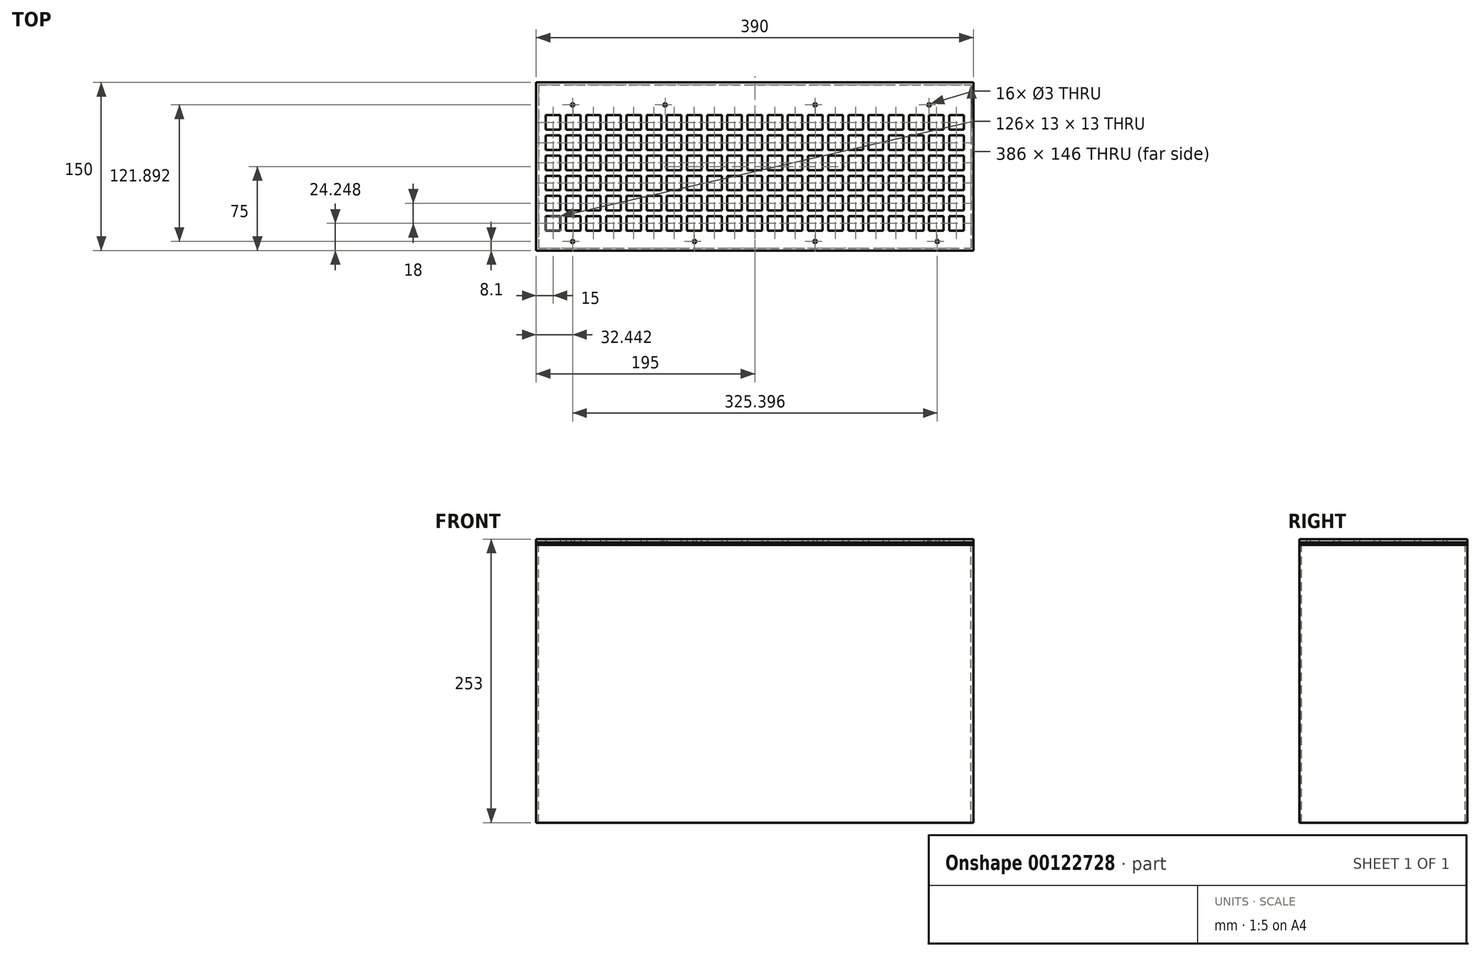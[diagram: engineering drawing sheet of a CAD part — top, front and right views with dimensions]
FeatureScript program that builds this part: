
annotation { "Feature Type Name" : "Feature", "Feature Type Description" : "" }
export const myFeature = defineFeature(function(context is Context, id is Id, definition is map)
    precondition{}
    {
        {
            var Q0;
            Q0=qCreatedBy(makeId("Top.planeOp"),FACE);
            var sketch = newSketch(context, id + "F0", { "sketchPlane" : qUnion([Q0])});
            skLineSegment(sketch, "E0.bottom", {"start": v(0, 0) * mm, "end": v(390, 0) * mm});
            skLineSegment(sketch, "E0.top", {"start": v(0, -150) * mm, "end": v(390, -150) * mm});
            skLineSegment(sketch, "E0.left", {"start": v(0, 0) * mm, "end": v(0, -150) * mm});
            skLineSegment(sketch, "E0.right", {"start": v(390, 0) * mm, "end": v(390, -150) * mm});
            skLineSegment(sketch, "E1.bottom", {"start": v(8.5, -29.25) * mm, "end": v(21.5, -29.25) * mm});
            skLineSegment(sketch, "E1.top", {"start": v(8.5, -42.25) * mm, "end": v(21.5, -42.25) * mm});
            skLineSegment(sketch, "E1.left", {"start": v(8.5, -29.25) * mm, "end": v(8.5, -42.25) * mm});
            skLineSegment(sketch, "E1.right", {"start": v(21.5, -29.25) * mm, "end": v(21.5, -42.25) * mm});
            skLineSegment(sketch, "E2.bottom", {"start": v(8.5, -47.25) * mm, "end": v(21.5, -47.25) * mm});
            skLineSegment(sketch, "E2.top", {"start": v(8.5, -60.25) * mm, "end": v(21.5, -60.25) * mm});
            skLineSegment(sketch, "E2.left", {"start": v(8.5, -47.25) * mm, "end": v(8.5, -60.25) * mm});
            skLineSegment(sketch, "E2.right", {"start": v(21.5, -47.25) * mm, "end": v(21.5, -60.25) * mm});
            skLineSegment(sketch, "E3.bottom", {"start": v(8.5, -65.25) * mm, "end": v(21.5, -65.25) * mm});
            skLineSegment(sketch, "E3.top", {"start": v(8.5, -78.25) * mm, "end": v(21.5, -78.25) * mm});
            skLineSegment(sketch, "E3.left", {"start": v(8.5, -65.25) * mm, "end": v(8.5, -78.25) * mm});
            skLineSegment(sketch, "E3.right", {"start": v(21.5, -65.25) * mm, "end": v(21.5, -78.25) * mm});
            skLineSegment(sketch, "E4.bottom", {"start": v(8.5, -83.25) * mm, "end": v(21.5, -83.25) * mm});
            skLineSegment(sketch, "E4.top", {"start": v(8.5, -96.25) * mm, "end": v(21.5, -96.25) * mm});
            skLineSegment(sketch, "E4.left", {"start": v(8.5, -83.25) * mm, "end": v(8.5, -96.25) * mm});
            skLineSegment(sketch, "E4.right", {"start": v(21.5, -83.25) * mm, "end": v(21.5, -96.25) * mm});
            skLineSegment(sketch, "E5.bottom", {"start": v(8.5, -101.25) * mm, "end": v(21.5, -101.25) * mm});
            skLineSegment(sketch, "E5.top", {"start": v(8.5, -114.25) * mm, "end": v(21.5, -114.25) * mm});
            skLineSegment(sketch, "E5.left", {"start": v(8.5, -101.25) * mm, "end": v(8.5, -114.25) * mm});
            skLineSegment(sketch, "E5.right", {"start": v(21.5, -101.25) * mm, "end": v(21.5, -114.25) * mm});
            skLineSegment(sketch, "E6.bottom", {"start": v(8.5, -119.25) * mm, "end": v(21.5, -119.25) * mm});
            skLineSegment(sketch, "E6.top", {"start": v(8.5, -132.25) * mm, "end": v(21.5, -132.25) * mm});
            skLineSegment(sketch, "E6.left", {"start": v(8.5, -119.25) * mm, "end": v(8.5, -132.25) * mm});
            skLineSegment(sketch, "E6.right", {"start": v(21.5, -119.25) * mm, "end": v(21.5, -132.25) * mm});
            skLineSegment(sketch, "E7", {"start": v(24, -21.56) * mm, "end": v(24, -144.75) * mm, "construction": true});
            skLineSegment(sketch, "E8.MirrorCS", {"start": v(39.5, -47.25) * mm, "end": v(39.5, -60.25) * mm});
            skLineSegment(sketch, "E9.MirrorCS", {"start": v(39.5, -60.25) * mm, "end": v(26.5, -60.25) * mm});
            skLineSegment(sketch, "E10.MirrorCS", {"start": v(39.5, -132.25) * mm, "end": v(26.5, -132.25) * mm});
            skLineSegment(sketch, "E11.MirrorCS", {"start": v(39.5, -119.25) * mm, "end": v(26.5, -119.25) * mm});
            skLineSegment(sketch, "E12.MirrorCS", {"start": v(39.5, -119.25) * mm, "end": v(39.5, -132.25) * mm});
            skLineSegment(sketch, "E13.MirrorCS", {"start": v(26.5, -29.25) * mm, "end": v(26.5, -42.25) * mm});
            skLineSegment(sketch, "E14.MirrorCS", {"start": v(39.5, -29.25) * mm, "end": v(26.5, -29.25) * mm});
            skLineSegment(sketch, "E15.MirrorCS", {"start": v(39.5, -101.25) * mm, "end": v(26.5, -101.25) * mm});
            skLineSegment(sketch, "E16.MirrorCS", {"start": v(26.5, -83.25) * mm, "end": v(26.5, -96.25) * mm});
            skLineSegment(sketch, "E17.MirrorCS", {"start": v(39.5, -83.25) * mm, "end": v(39.5, -96.25) * mm});
            skLineSegment(sketch, "E18.MirrorCS", {"start": v(39.5, -96.25) * mm, "end": v(26.5, -96.25) * mm});
            skLineSegment(sketch, "E19.MirrorCS", {"start": v(39.5, -83.25) * mm, "end": v(26.5, -83.25) * mm});
            skLineSegment(sketch, "E20.MirrorCS", {"start": v(26.5, -65.25) * mm, "end": v(26.5, -78.25) * mm});
            skLineSegment(sketch, "E21.MirrorCS", {"start": v(39.5, -65.25) * mm, "end": v(39.5, -78.25) * mm});
            skLineSegment(sketch, "E22.MirrorCS", {"start": v(39.5, -65.25) * mm, "end": v(26.5, -65.25) * mm});
            skLineSegment(sketch, "E23.MirrorCS", {"start": v(39.5, -78.25) * mm, "end": v(26.5, -78.25) * mm});
            skLineSegment(sketch, "E24.MirrorCS", {"start": v(26.5, -101.25) * mm, "end": v(26.5, -114.25) * mm});
            skLineSegment(sketch, "E25.MirrorCS", {"start": v(26.5, -47.25) * mm, "end": v(26.5, -60.25) * mm});
            skLineSegment(sketch, "E26.MirrorCS", {"start": v(26.5, -119.25) * mm, "end": v(26.5, -132.25) * mm});
            skLineSegment(sketch, "E27.MirrorCS", {"start": v(39.5, -101.25) * mm, "end": v(39.5, -114.25) * mm});
            skLineSegment(sketch, "E28.MirrorCS", {"start": v(39.5, -29.25) * mm, "end": v(39.5, -42.25) * mm});
            skLineSegment(sketch, "E29.MirrorCS", {"start": v(39.5, -114.25) * mm, "end": v(26.5, -114.25) * mm});
            skLineSegment(sketch, "E30.MirrorCS", {"start": v(39.5, -47.25) * mm, "end": v(26.5, -47.25) * mm});
            skLineSegment(sketch, "E31.MirrorCS", {"start": v(39.5, -42.25) * mm, "end": v(26.5, -42.25) * mm});
            skLineSegment(sketch, "E32", {"start": v(42, -21.56) * mm, "end": v(42, -144.75) * mm, "construction": true});
            skLineSegment(sketch, "E33.MirrorCS", {"start": v(57.5, -119.25) * mm, "end": v(57.5, -132.25) * mm});
            skLineSegment(sketch, "E34.MirrorCS", {"start": v(44.5, -29.25) * mm, "end": v(44.5, -42.25) * mm});
            skLineSegment(sketch, "E35.MirrorCS", {"start": v(44.5, -119.25) * mm, "end": v(44.5, -132.25) * mm});
            skLineSegment(sketch, "E36.MirrorCS", {"start": v(44.5, -114.25) * mm, "end": v(57.5, -114.25) * mm});
            skLineSegment(sketch, "E37.MirrorCS", {"start": v(75.5, -83.25) * mm, "end": v(75.5, -96.25) * mm});
            skLineSegment(sketch, "E38.MirrorCS", {"start": v(62.5, -65.25) * mm, "end": v(62.5, -78.25) * mm});
            skLineSegment(sketch, "E39.MirrorCS", {"start": v(75.5, -114.25) * mm, "end": v(62.5, -114.25) * mm});
            skLineSegment(sketch, "E40.MirrorCS", {"start": v(75.5, -42.25) * mm, "end": v(62.5, -42.25) * mm});
            skLineSegment(sketch, "E41.MirrorCS", {"start": v(57.5, -83.25) * mm, "end": v(57.5, -96.25) * mm});
            skLineSegment(sketch, "E42.MirrorCS", {"start": v(75.5, -101.25) * mm, "end": v(75.5, -114.25) * mm});
            skLineSegment(sketch, "E43.MirrorCS", {"start": v(75.5, -29.25) * mm, "end": v(75.5, -42.25) * mm});
            skLineSegment(sketch, "E44.MirrorCS", {"start": v(44.5, -83.25) * mm, "end": v(44.5, -96.25) * mm});
            skLineSegment(sketch, "E45.MirrorCS", {"start": v(44.5, -96.25) * mm, "end": v(57.5, -96.25) * mm});
            skLineSegment(sketch, "E46.MirrorCS", {"start": v(62.5, -101.25) * mm, "end": v(62.5, -114.25) * mm});
            skLineSegment(sketch, "E47.MirrorCS", {"start": v(62.5, -29.25) * mm, "end": v(62.5, -42.25) * mm});
            skLineSegment(sketch, "E48.MirrorCS", {"start": v(44.5, -83.25) * mm, "end": v(57.5, -83.25) * mm});
            skLineSegment(sketch, "E49.MirrorCS", {"start": v(75.5, -119.25) * mm, "end": v(62.5, -119.25) * mm});
            skLineSegment(sketch, "E50.MirrorCS", {"start": v(75.5, -47.25) * mm, "end": v(62.5, -47.25) * mm});
            skLineSegment(sketch, "E51.MirrorCS", {"start": v(57.5, -65.25) * mm, "end": v(57.5, -78.25) * mm});
            skLineSegment(sketch, "E52.MirrorCS", {"start": v(75.5, -60.25) * mm, "end": v(62.5, -60.25) * mm});
            skLineSegment(sketch, "E53.MirrorCS", {"start": v(75.5, -132.25) * mm, "end": v(62.5, -132.25) * mm});
            skLineSegment(sketch, "E54.MirrorCS", {"start": v(44.5, -132.25) * mm, "end": v(57.5, -132.25) * mm});
            skLineSegment(sketch, "E55.MirrorCS", {"start": v(75.5, -78.25) * mm, "end": v(62.5, -78.25) * mm});
            skLineSegment(sketch, "E56.MirrorCS", {"start": v(57.5, -101.25) * mm, "end": v(57.5, -114.25) * mm});
            skLineSegment(sketch, "E57.MirrorCS", {"start": v(44.5, -47.25) * mm, "end": v(44.5, -60.25) * mm});
            skLineSegment(sketch, "E58.MirrorCS", {"start": v(44.5, -65.25) * mm, "end": v(44.5, -78.25) * mm});
            skLineSegment(sketch, "E59.MirrorCS", {"start": v(75.5, -119.25) * mm, "end": v(75.5, -132.25) * mm});
            skLineSegment(sketch, "E60.MirrorCS", {"start": v(75.5, -47.25) * mm, "end": v(75.5, -60.25) * mm});
            skLineSegment(sketch, "E61.MirrorCS", {"start": v(75.5, -65.25) * mm, "end": v(75.5, -78.25) * mm});
            skLineSegment(sketch, "E62.MirrorCS", {"start": v(57.5, -47.25) * mm, "end": v(57.5, -60.25) * mm});
            skLineSegment(sketch, "E63.MirrorCS", {"start": v(44.5, -60.25) * mm, "end": v(57.5, -60.25) * mm});
            skLineSegment(sketch, "E64.MirrorCS", {"start": v(44.5, -65.25) * mm, "end": v(57.5, -65.25) * mm});
            skLineSegment(sketch, "E65.MirrorCS", {"start": v(62.5, -119.25) * mm, "end": v(62.5, -132.25) * mm});
            skLineSegment(sketch, "E66.MirrorCS", {"start": v(62.5, -47.25) * mm, "end": v(62.5, -60.25) * mm});
            skLineSegment(sketch, "E67.MirrorCS", {"start": v(44.5, -119.25) * mm, "end": v(57.5, -119.25) * mm});
            skLineSegment(sketch, "E68.MirrorCS", {"start": v(44.5, -101.25) * mm, "end": v(44.5, -114.25) * mm});
            skLineSegment(sketch, "E69.MirrorCS", {"start": v(75.5, -83.25) * mm, "end": v(62.5, -83.25) * mm});
            skLineSegment(sketch, "E70.MirrorCS", {"start": v(44.5, -101.25) * mm, "end": v(57.5, -101.25) * mm});
            skLineSegment(sketch, "E71.MirrorCS", {"start": v(75.5, -96.25) * mm, "end": v(62.5, -96.25) * mm});
            skLineSegment(sketch, "E72.MirrorCS", {"start": v(44.5, -78.25) * mm, "end": v(57.5, -78.25) * mm});
            skLineSegment(sketch, "E73.MirrorCS", {"start": v(75.5, -65.25) * mm, "end": v(62.5, -65.25) * mm});
            skLineSegment(sketch, "E74.MirrorCS", {"start": v(44.5, -42.25) * mm, "end": v(57.5, -42.25) * mm});
            skLineSegment(sketch, "E75.MirrorCS", {"start": v(44.5, -47.25) * mm, "end": v(57.5, -47.25) * mm});
            skLineSegment(sketch, "E76.MirrorCS", {"start": v(62.5, -83.25) * mm, "end": v(62.5, -96.25) * mm});
            skLineSegment(sketch, "E77.MirrorCS", {"start": v(75.5, -29.25) * mm, "end": v(62.5, -29.25) * mm});
            skLineSegment(sketch, "E78.MirrorCS", {"start": v(44.5, -29.25) * mm, "end": v(57.5, -29.25) * mm});
            skLineSegment(sketch, "E79.MirrorCS", {"start": v(75.5, -101.25) * mm, "end": v(62.5, -101.25) * mm});
            skLineSegment(sketch, "E80.MirrorCS", {"start": v(57.5, -29.25) * mm, "end": v(57.5, -42.25) * mm});
            skLineSegment(sketch, "E81", {"start": v(78, -21.56) * mm, "end": v(78, -144.75) * mm, "construction": true});
            skLineSegment(sketch, "E82.MirrorCS", {"start": v(111.5, -29.25) * mm, "end": v(111.5, -42.25) * mm});
            skLineSegment(sketch, "E83.MirrorCS", {"start": v(116.5, -83.25) * mm, "end": v(116.5, -96.25) * mm});
            skLineSegment(sketch, "E84.MirrorCS", {"start": v(93.5, -119.25) * mm, "end": v(93.5, -132.25) * mm});
            skLineSegment(sketch, "E85.MirrorCS", {"start": v(147.5, -47.25) * mm, "end": v(134.5, -47.25) * mm});
            skLineSegment(sketch, "E86.MirrorCS", {"start": v(147.5, -101.25) * mm, "end": v(134.5, -101.25) * mm});
            skLineSegment(sketch, "E87.MirrorCS", {"start": v(147.5, -29.25) * mm, "end": v(134.5, -29.25) * mm});
            skLineSegment(sketch, "E88.MirrorCS", {"start": v(147.5, -119.25) * mm, "end": v(134.5, -119.25) * mm});
            skLineSegment(sketch, "E89.MirrorCS", {"start": v(116.5, -83.25) * mm, "end": v(129.5, -83.25) * mm});
            skLineSegment(sketch, "E90.MirrorCS", {"start": v(111.5, -119.25) * mm, "end": v(111.5, -132.25) * mm});
            skLineSegment(sketch, "E91.MirrorCS", {"start": v(98.5, -29.25) * mm, "end": v(98.5, -42.25) * mm});
            skLineSegment(sketch, "E92.MirrorCS", {"start": v(129.5, -83.25) * mm, "end": v(129.5, -96.25) * mm});
            skLineSegment(sketch, "E93.MirrorCS", {"start": v(147.5, -65.25) * mm, "end": v(147.5, -78.25) * mm});
            skLineSegment(sketch, "E94.MirrorCS", {"start": v(116.5, -29.25) * mm, "end": v(129.5, -29.25) * mm});
            skLineSegment(sketch, "E95.MirrorCS", {"start": v(116.5, -47.25) * mm, "end": v(129.5, -47.25) * mm});
            skLineSegment(sketch, "E96.MirrorCS", {"start": v(93.5, -101.25) * mm, "end": v(93.5, -114.25) * mm});
            skLineSegment(sketch, "E97.MirrorCS", {"start": v(98.5, -47.25) * mm, "end": v(98.5, -60.25) * mm});
            skLineSegment(sketch, "E98.MirrorCS", {"start": v(93.5, -47.25) * mm, "end": v(93.5, -60.25) * mm});
            skLineSegment(sketch, "E99.MirrorCS", {"start": v(134.5, -83.25) * mm, "end": v(134.5, -96.25) * mm});
            skLineSegment(sketch, "E100.MirrorCS", {"start": v(111.5, -29.25) * mm, "end": v(98.5, -29.25) * mm});
            skLineSegment(sketch, "E101.MirrorCS", {"start": v(80.5, -29.25) * mm, "end": v(93.5, -29.25) * mm});
            skLineSegment(sketch, "E102.MirrorCS", {"start": v(129.5, -29.25) * mm, "end": v(129.5, -42.25) * mm});
            skLineSegment(sketch, "E103.MirrorCS", {"start": v(116.5, -114.25) * mm, "end": v(129.5, -114.25) * mm});
            skLineSegment(sketch, "E104.MirrorCS", {"start": v(111.5, -96.25) * mm, "end": v(98.5, -96.25) * mm});
            skLineSegment(sketch, "E105.MirrorCS", {"start": v(80.5, -65.25) * mm, "end": v(80.5, -78.25) * mm});
            skLineSegment(sketch, "E106.MirrorCS", {"start": v(93.5, -83.25) * mm, "end": v(93.5, -96.25) * mm});
            skLineSegment(sketch, "E107.MirrorCS", {"start": v(116.5, -119.25) * mm, "end": v(116.5, -132.25) * mm});
            skLineSegment(sketch, "E108.MirrorCS", {"start": v(116.5, -29.25) * mm, "end": v(116.5, -42.25) * mm});
            skLineSegment(sketch, "E109.MirrorCS", {"start": v(111.5, -83.25) * mm, "end": v(111.5, -96.25) * mm});
            skLineSegment(sketch, "E110.MirrorCS", {"start": v(80.5, -47.25) * mm, "end": v(80.5, -60.25) * mm});
            skLineSegment(sketch, "E111.MirrorCS", {"start": v(147.5, -96.25) * mm, "end": v(134.5, -96.25) * mm});
            skLineSegment(sketch, "E112.MirrorCS", {"start": v(134.5, -29.25) * mm, "end": v(134.5, -42.25) * mm});
            skLineSegment(sketch, "E113.MirrorCS", {"start": v(80.5, -132.25) * mm, "end": v(93.5, -132.25) * mm});
            skLineSegment(sketch, "E114.MirrorCS", {"start": v(80.5, -83.25) * mm, "end": v(93.5, -83.25) * mm});
            skLineSegment(sketch, "E115.MirrorCS", {"start": v(147.5, -47.25) * mm, "end": v(147.5, -60.25) * mm});
            skLineSegment(sketch, "E116.MirrorCS", {"start": v(147.5, -119.25) * mm, "end": v(147.5, -132.25) * mm});
            skLineSegment(sketch, "E117.MirrorCS", {"start": v(116.5, -65.25) * mm, "end": v(116.5, -78.25) * mm});
            skLineSegment(sketch, "E118.MirrorCS", {"start": v(80.5, -83.25) * mm, "end": v(80.5, -96.25) * mm});
            skLineSegment(sketch, "E119.MirrorCS", {"start": v(134.5, -101.25) * mm, "end": v(134.5, -114.25) * mm});
            skLineSegment(sketch, "E120.MirrorCS", {"start": v(111.5, -47.25) * mm, "end": v(98.5, -47.25) * mm});
            skLineSegment(sketch, "E121.MirrorCS", {"start": v(116.5, -101.25) * mm, "end": v(116.5, -114.25) * mm});
            skLineSegment(sketch, "E122.MirrorCS", {"start": v(116.5, -119.25) * mm, "end": v(129.5, -119.25) * mm});
            skLineSegment(sketch, "E123.MirrorCS", {"start": v(80.5, -29.25) * mm, "end": v(80.5, -42.25) * mm});
            skLineSegment(sketch, "E124.MirrorCS", {"start": v(80.5, -119.25) * mm, "end": v(80.5, -132.25) * mm});
            skLineSegment(sketch, "E125.MirrorCS", {"start": v(147.5, -83.25) * mm, "end": v(134.5, -83.25) * mm});
            skLineSegment(sketch, "E126.MirrorCS", {"start": v(111.5, -42.25) * mm, "end": v(98.5, -42.25) * mm});
            skLineSegment(sketch, "E127.MirrorCS", {"start": v(116.5, -132.25) * mm, "end": v(129.5, -132.25) * mm});
            skLineSegment(sketch, "E128.MirrorCS", {"start": v(129.5, -119.25) * mm, "end": v(129.5, -132.25) * mm});
            skLineSegment(sketch, "E129.MirrorCS", {"start": v(80.5, -101.25) * mm, "end": v(80.5, -114.25) * mm});
            skLineSegment(sketch, "E130.MirrorCS", {"start": v(111.5, -65.25) * mm, "end": v(111.5, -78.25) * mm});
            skLineSegment(sketch, "E131.MirrorCS", {"start": v(80.5, -60.25) * mm, "end": v(93.5, -60.25) * mm});
            skLineSegment(sketch, "E132.MirrorCS", {"start": v(111.5, -101.25) * mm, "end": v(111.5, -114.25) * mm});
            skLineSegment(sketch, "E133.MirrorCS", {"start": v(134.5, -65.25) * mm, "end": v(134.5, -78.25) * mm});
            skLineSegment(sketch, "E134.MirrorCS", {"start": v(147.5, -60.25) * mm, "end": v(134.5, -60.25) * mm});
            skLineSegment(sketch, "E135.MirrorCS", {"start": v(147.5, -132.25) * mm, "end": v(134.5, -132.25) * mm});
            skLineSegment(sketch, "E136.MirrorCS", {"start": v(129.5, -65.25) * mm, "end": v(129.5, -78.25) * mm});
            skLineSegment(sketch, "E137.MirrorCS", {"start": v(111.5, -114.25) * mm, "end": v(98.5, -114.25) * mm});
            skLineSegment(sketch, "E138.MirrorCS", {"start": v(80.5, -65.25) * mm, "end": v(93.5, -65.25) * mm});
            skLineSegment(sketch, "E139.MirrorCS", {"start": v(116.5, -60.25) * mm, "end": v(129.5, -60.25) * mm});
            skLineSegment(sketch, "E140.MirrorCS", {"start": v(129.5, -47.25) * mm, "end": v(129.5, -60.25) * mm});
            skLineSegment(sketch, "E141.MirrorCS", {"start": v(98.5, -83.25) * mm, "end": v(98.5, -96.25) * mm});
            skLineSegment(sketch, "E142.MirrorCS", {"start": v(111.5, -47.25) * mm, "end": v(111.5, -60.25) * mm});
            skLineSegment(sketch, "E143.MirrorCS", {"start": v(80.5, -47.25) * mm, "end": v(93.5, -47.25) * mm});
            skLineSegment(sketch, "E144.MirrorCS", {"start": v(116.5, -96.25) * mm, "end": v(129.5, -96.25) * mm});
            skLineSegment(sketch, "E145.MirrorCS", {"start": v(111.5, -119.25) * mm, "end": v(98.5, -119.25) * mm});
            skLineSegment(sketch, "E146.MirrorCS", {"start": v(98.5, -65.25) * mm, "end": v(98.5, -78.25) * mm});
            skLineSegment(sketch, "E147.MirrorCS", {"start": v(111.5, -60.25) * mm, "end": v(98.5, -60.25) * mm});
            skLineSegment(sketch, "E148.MirrorCS", {"start": v(147.5, -83.25) * mm, "end": v(147.5, -96.25) * mm});
            skLineSegment(sketch, "E149.MirrorCS", {"start": v(111.5, -65.25) * mm, "end": v(98.5, -65.25) * mm});
            skLineSegment(sketch, "E150.MirrorCS", {"start": v(111.5, -83.25) * mm, "end": v(98.5, -83.25) * mm});
            skLineSegment(sketch, "E151.MirrorCS", {"start": v(116.5, -42.25) * mm, "end": v(129.5, -42.25) * mm});
            skLineSegment(sketch, "E152.MirrorCS", {"start": v(147.5, -42.25) * mm, "end": v(134.5, -42.25) * mm});
            skLineSegment(sketch, "E153.MirrorCS", {"start": v(147.5, -114.25) * mm, "end": v(134.5, -114.25) * mm});
            skLineSegment(sketch, "E154.MirrorCS", {"start": v(98.5, -101.25) * mm, "end": v(98.5, -114.25) * mm});
            skLineSegment(sketch, "E155.MirrorCS", {"start": v(80.5, -42.25) * mm, "end": v(93.5, -42.25) * mm});
            skLineSegment(sketch, "E156.MirrorCS", {"start": v(129.5, -101.25) * mm, "end": v(129.5, -114.25) * mm});
            skLineSegment(sketch, "E157.MirrorCS", {"start": v(116.5, -47.25) * mm, "end": v(116.5, -60.25) * mm});
            skLineSegment(sketch, "E158.MirrorCS", {"start": v(111.5, -78.25) * mm, "end": v(98.5, -78.25) * mm});
            skLineSegment(sketch, "E159.MirrorCS", {"start": v(147.5, -101.25) * mm, "end": v(147.5, -114.25) * mm});
            skLineSegment(sketch, "E160.MirrorCS", {"start": v(93.5, -29.25) * mm, "end": v(93.5, -42.25) * mm});
            skLineSegment(sketch, "E161.MirrorCS", {"start": v(116.5, -101.25) * mm, "end": v(129.5, -101.25) * mm});
            skLineSegment(sketch, "E162.MirrorCS", {"start": v(80.5, -101.25) * mm, "end": v(93.5, -101.25) * mm});
            skLineSegment(sketch, "E163.MirrorCS", {"start": v(147.5, -29.25) * mm, "end": v(147.5, -42.25) * mm});
            skLineSegment(sketch, "E164.MirrorCS", {"start": v(80.5, -119.25) * mm, "end": v(93.5, -119.25) * mm});
            skLineSegment(sketch, "E165.MirrorCS", {"start": v(98.5, -119.25) * mm, "end": v(98.5, -132.25) * mm});
            skLineSegment(sketch, "E166.MirrorCS", {"start": v(147.5, -78.25) * mm, "end": v(134.5, -78.25) * mm});
            skLineSegment(sketch, "E167.MirrorCS", {"start": v(147.5, -65.25) * mm, "end": v(134.5, -65.25) * mm});
            skLineSegment(sketch, "E168.MirrorCS", {"start": v(80.5, -78.25) * mm, "end": v(93.5, -78.25) * mm});
            skLineSegment(sketch, "E169.MirrorCS", {"start": v(80.5, -96.25) * mm, "end": v(93.5, -96.25) * mm});
            skLineSegment(sketch, "E170.MirrorCS", {"start": v(116.5, -78.25) * mm, "end": v(129.5, -78.25) * mm});
            skLineSegment(sketch, "E171.MirrorCS", {"start": v(80.5, -114.25) * mm, "end": v(93.5, -114.25) * mm});
            skLineSegment(sketch, "E172.MirrorCS", {"start": v(134.5, -119.25) * mm, "end": v(134.5, -132.25) * mm});
            skLineSegment(sketch, "E173.MirrorCS", {"start": v(116.5, -65.25) * mm, "end": v(129.5, -65.25) * mm});
            skLineSegment(sketch, "E174.MirrorCS", {"start": v(93.5, -65.25) * mm, "end": v(93.5, -78.25) * mm});
            skLineSegment(sketch, "E175.MirrorCS", {"start": v(134.5, -47.25) * mm, "end": v(134.5, -60.25) * mm});
            skLineSegment(sketch, "E176.MirrorCS", {"start": v(111.5, -101.25) * mm, "end": v(98.5, -101.25) * mm});
            skLineSegment(sketch, "E177.MirrorCS", {"start": v(111.5, -132.25) * mm, "end": v(98.5, -132.25) * mm});
            skLineSegment(sketch, "E178", {"start": v(150, -21.56) * mm, "end": v(150, -144.75) * mm, "construction": true});
            skLineSegment(sketch, "E179.MirrorCS", {"start": v(291.5, -83.25) * mm, "end": v(291.5, -96.25) * mm});
            skLineSegment(sketch, "E180.MirrorCS", {"start": v(291.5, -101.25) * mm, "end": v(278.5, -101.25) * mm});
            skLineSegment(sketch, "E181.MirrorCS", {"start": v(291.5, -29.25) * mm, "end": v(278.5, -29.25) * mm});
            skLineSegment(sketch, "E182.MirrorCS", {"start": v(291.5, -29.25) * mm, "end": v(291.5, -42.25) * mm});
            skLineSegment(sketch, "E183.MirrorCS", {"start": v(291.5, -47.25) * mm, "end": v(291.5, -60.25) * mm});
            skLineSegment(sketch, "E184.MirrorCS", {"start": v(291.5, -119.25) * mm, "end": v(291.5, -132.25) * mm});
            skLineSegment(sketch, "E185.MirrorCS", {"start": v(291.5, -65.25) * mm, "end": v(278.5, -65.25) * mm});
            skLineSegment(sketch, "E186.MirrorCS", {"start": v(291.5, -65.25) * mm, "end": v(291.5, -78.25) * mm});
            skLineSegment(sketch, "E187.MirrorCS", {"start": v(260.5, -119.25) * mm, "end": v(260.5, -132.25) * mm});
            skLineSegment(sketch, "E188.MirrorCS", {"start": v(255.5, -83.25) * mm, "end": v(255.5, -96.25) * mm});
            skLineSegment(sketch, "E189.MirrorCS", {"start": v(170.5, -101.25) * mm, "end": v(170.5, -114.25) * mm});
            skLineSegment(sketch, "E190.MirrorCS", {"start": v(224.5, -65.25) * mm, "end": v(224.5, -78.25) * mm});
            skLineSegment(sketch, "E191.MirrorCS", {"start": v(255.5, -96.25) * mm, "end": v(242.5, -96.25) * mm});
            skLineSegment(sketch, "E192.MirrorCS", {"start": v(260.5, -114.25) * mm, "end": v(273.5, -114.25) * mm});
            skLineSegment(sketch, "E193.MirrorCS", {"start": v(273.5, -29.25) * mm, "end": v(273.5, -42.25) * mm});
            skLineSegment(sketch, "E194.MirrorCS", {"start": v(152.5, -83.25) * mm, "end": v(165.5, -83.25) * mm});
            skLineSegment(sketch, "E195.MirrorCS", {"start": v(152.5, -65.25) * mm, "end": v(152.5, -78.25) * mm});
            skLineSegment(sketch, "E196.MirrorCS", {"start": v(224.5, -29.25) * mm, "end": v(237.5, -29.25) * mm});
            skLineSegment(sketch, "E197.MirrorCS", {"start": v(183.5, -47.25) * mm, "end": v(183.5, -60.25) * mm});
            skLineSegment(sketch, "E198.MirrorCS", {"start": v(152.5, -101.25) * mm, "end": v(152.5, -114.25) * mm});
            skLineSegment(sketch, "E199.MirrorCS", {"start": v(219.5, -47.25) * mm, "end": v(206.5, -47.25) * mm});
            skLineSegment(sketch, "E200.MirrorCS", {"start": v(219.5, -119.25) * mm, "end": v(219.5, -132.25) * mm});
            skLineSegment(sketch, "E201.MirrorCS", {"start": v(237.5, -29.25) * mm, "end": v(237.5, -42.25) * mm});
            skLineSegment(sketch, "E202.MirrorCS", {"start": v(260.5, -42.25) * mm, "end": v(273.5, -42.25) * mm});
            skLineSegment(sketch, "E203.MirrorCS", {"start": v(260.5, -101.25) * mm, "end": v(273.5, -101.25) * mm});
            skLineSegment(sketch, "E204.MirrorCS", {"start": v(183.5, -132.25) * mm, "end": v(170.5, -132.25) * mm});
            skLineSegment(sketch, "E205.MirrorCS", {"start": v(152.5, -96.25) * mm, "end": v(165.5, -96.25) * mm});
            skLineSegment(sketch, "E206.MirrorCS", {"start": v(183.5, -47.25) * mm, "end": v(170.5, -47.25) * mm});
            skLineSegment(sketch, "E207.MirrorCS", {"start": v(224.5, -101.25) * mm, "end": v(237.5, -101.25) * mm});
            skLineSegment(sketch, "E208.MirrorCS", {"start": v(291.5, -114.25) * mm, "end": v(278.5, -114.25) * mm});
            skLineSegment(sketch, "E209.MirrorCS", {"start": v(291.5, -42.25) * mm, "end": v(278.5, -42.25) * mm});
            skLineSegment(sketch, "E210.MirrorCS", {"start": v(255.5, -65.25) * mm, "end": v(242.5, -65.25) * mm});
            skLineSegment(sketch, "E211.MirrorCS", {"start": v(255.5, -83.25) * mm, "end": v(242.5, -83.25) * mm});
            skLineSegment(sketch, "E212.MirrorCS", {"start": v(273.5, -83.25) * mm, "end": v(273.5, -96.25) * mm});
            skLineSegment(sketch, "E213.MirrorCS", {"start": v(165.5, -29.25) * mm, "end": v(165.5, -42.25) * mm});
            skLineSegment(sketch, "E214.MirrorCS", {"start": v(242.5, -29.25) * mm, "end": v(242.5, -42.25) * mm});
            skLineSegment(sketch, "E215.MirrorCS", {"start": v(206.5, -101.25) * mm, "end": v(206.5, -114.25) * mm});
            skLineSegment(sketch, "E216.MirrorCS", {"start": v(188.5, -101.25) * mm, "end": v(201.5, -101.25) * mm});
            skLineSegment(sketch, "E217.MirrorCS", {"start": v(206.5, -29.25) * mm, "end": v(206.5, -42.25) * mm});
            skLineSegment(sketch, "E218.MirrorCS", {"start": v(183.5, -96.25) * mm, "end": v(170.5, -96.25) * mm});
            skLineSegment(sketch, "E219.MirrorCS", {"start": v(291.5, -101.25) * mm, "end": v(291.5, -114.25) * mm});
            skLineSegment(sketch, "E220.MirrorCS", {"start": v(237.5, -119.25) * mm, "end": v(237.5, -132.25) * mm});
            skLineSegment(sketch, "E221.MirrorCS", {"start": v(224.5, -119.25) * mm, "end": v(237.5, -119.25) * mm});
            skLineSegment(sketch, "E222.MirrorCS", {"start": v(242.5, -119.25) * mm, "end": v(242.5, -132.25) * mm});
            skLineSegment(sketch, "E223.MirrorCS", {"start": v(260.5, -83.25) * mm, "end": v(260.5, -96.25) * mm});
            skLineSegment(sketch, "E224.MirrorCS", {"start": v(219.5, -101.25) * mm, "end": v(219.5, -114.25) * mm});
            skLineSegment(sketch, "E225.MirrorCS", {"start": v(219.5, -132.25) * mm, "end": v(206.5, -132.25) * mm});
            skLineSegment(sketch, "E226.MirrorCS", {"start": v(201.5, -47.25) * mm, "end": v(201.5, -60.25) * mm});
            skLineSegment(sketch, "E227.MirrorCS", {"start": v(188.5, -132.25) * mm, "end": v(201.5, -132.25) * mm});
            skLineSegment(sketch, "E228.MirrorCS", {"start": v(183.5, -101.25) * mm, "end": v(170.5, -101.25) * mm});
            skLineSegment(sketch, "E229.MirrorCS", {"start": v(188.5, -119.25) * mm, "end": v(201.5, -119.25) * mm});
            skLineSegment(sketch, "E230.MirrorCS", {"start": v(278.5, -65.25) * mm, "end": v(278.5, -78.25) * mm});
            skLineSegment(sketch, "E231.MirrorCS", {"start": v(255.5, -65.25) * mm, "end": v(255.5, -78.25) * mm});
            skLineSegment(sketch, "E232.MirrorCS", {"start": v(224.5, -101.25) * mm, "end": v(224.5, -114.25) * mm});
            skLineSegment(sketch, "E233.MirrorCS", {"start": v(273.5, -119.25) * mm, "end": v(273.5, -132.25) * mm});
            skLineSegment(sketch, "E234.MirrorCS", {"start": v(260.5, -132.25) * mm, "end": v(273.5, -132.25) * mm});
            skLineSegment(sketch, "E235.MirrorCS", {"start": v(206.5, -83.25) * mm, "end": v(206.5, -96.25) * mm});
            skLineSegment(sketch, "E236.MirrorCS", {"start": v(183.5, -119.25) * mm, "end": v(170.5, -119.25) * mm});
            skLineSegment(sketch, "E237.MirrorCS", {"start": v(170.5, -83.25) * mm, "end": v(170.5, -96.25) * mm});
            skLineSegment(sketch, "E238.MirrorCS", {"start": v(188.5, -119.25) * mm, "end": v(188.5, -132.25) * mm});
            skLineSegment(sketch, "E239.MirrorCS", {"start": v(183.5, -78.25) * mm, "end": v(170.5, -78.25) * mm});
            skLineSegment(sketch, "E240.MirrorCS", {"start": v(255.5, -42.25) * mm, "end": v(242.5, -42.25) * mm});
            skLineSegment(sketch, "E241.MirrorCS", {"start": v(201.5, -101.25) * mm, "end": v(201.5, -114.25) * mm});
            skLineSegment(sketch, "E242.MirrorCS", {"start": v(219.5, -65.25) * mm, "end": v(206.5, -65.25) * mm});
            skLineSegment(sketch, "E243.MirrorCS", {"start": v(255.5, -29.25) * mm, "end": v(255.5, -42.25) * mm});
            skLineSegment(sketch, "E244.MirrorCS", {"start": v(260.5, -96.25) * mm, "end": v(273.5, -96.25) * mm});
            skLineSegment(sketch, "E245.MirrorCS", {"start": v(291.5, -83.25) * mm, "end": v(278.5, -83.25) * mm});
            skLineSegment(sketch, "E246.MirrorCS", {"start": v(278.5, -29.25) * mm, "end": v(278.5, -42.25) * mm});
            skLineSegment(sketch, "E247.MirrorCS", {"start": v(278.5, -101.25) * mm, "end": v(278.5, -114.25) * mm});
            skLineSegment(sketch, "E248.MirrorCS", {"start": v(224.5, -119.25) * mm, "end": v(224.5, -132.25) * mm});
            skLineSegment(sketch, "E249.MirrorCS", {"start": v(224.5, -29.25) * mm, "end": v(224.5, -42.25) * mm});
            skLineSegment(sketch, "E250.MirrorCS", {"start": v(260.5, -101.25) * mm, "end": v(260.5, -114.25) * mm});
            skLineSegment(sketch, "E251.MirrorCS", {"start": v(260.5, -119.25) * mm, "end": v(273.5, -119.25) * mm});
            skLineSegment(sketch, "E252.MirrorCS", {"start": v(219.5, -29.25) * mm, "end": v(219.5, -42.25) * mm});
            skLineSegment(sketch, "E253.MirrorCS", {"start": v(206.5, -47.25) * mm, "end": v(206.5, -60.25) * mm});
            skLineSegment(sketch, "E254.MirrorCS", {"start": v(188.5, -29.25) * mm, "end": v(188.5, -42.25) * mm});
            skLineSegment(sketch, "E255.MirrorCS", {"start": v(237.5, -47.25) * mm, "end": v(237.5, -60.25) * mm});
            skLineSegment(sketch, "E256.MirrorCS", {"start": v(224.5, -47.25) * mm, "end": v(237.5, -47.25) * mm});
            skLineSegment(sketch, "E257.MirrorCS", {"start": v(201.5, -65.25) * mm, "end": v(201.5, -78.25) * mm});
            skLineSegment(sketch, "E258.MirrorCS", {"start": v(219.5, -101.25) * mm, "end": v(206.5, -101.25) * mm});
            skLineSegment(sketch, "E259.MirrorCS", {"start": v(188.5, -65.25) * mm, "end": v(188.5, -78.25) * mm});
            skLineSegment(sketch, "E260.MirrorCS", {"start": v(219.5, -83.25) * mm, "end": v(206.5, -83.25) * mm});
            skLineSegment(sketch, "E261.MirrorCS", {"start": v(183.5, -119.25) * mm, "end": v(183.5, -132.25) * mm});
            skLineSegment(sketch, "E262.MirrorCS", {"start": v(201.5, -29.25) * mm, "end": v(201.5, -42.25) * mm});
            skLineSegment(sketch, "E263.MirrorCS", {"start": v(255.5, -47.25) * mm, "end": v(242.5, -47.25) * mm});
            skLineSegment(sketch, "E264.MirrorCS", {"start": v(219.5, -114.25) * mm, "end": v(206.5, -114.25) * mm});
            skLineSegment(sketch, "E265.MirrorCS", {"start": v(219.5, -42.25) * mm, "end": v(206.5, -42.25) * mm});
            skLineSegment(sketch, "E266.MirrorCS", {"start": v(183.5, -60.25) * mm, "end": v(170.5, -60.25) * mm});
            skLineSegment(sketch, "E267.MirrorCS", {"start": v(170.5, -47.25) * mm, "end": v(170.5, -60.25) * mm});
            skLineSegment(sketch, "E268.MirrorCS", {"start": v(224.5, -47.25) * mm, "end": v(224.5, -60.25) * mm});
            skLineSegment(sketch, "E269.MirrorCS", {"start": v(291.5, -96.25) * mm, "end": v(278.5, -96.25) * mm});
            skLineSegment(sketch, "E270.MirrorCS", {"start": v(219.5, -83.25) * mm, "end": v(219.5, -96.25) * mm});
            skLineSegment(sketch, "E271.MirrorCS", {"start": v(152.5, -60.25) * mm, "end": v(165.5, -60.25) * mm});
            skLineSegment(sketch, "E272.MirrorCS", {"start": v(152.5, -78.25) * mm, "end": v(165.5, -78.25) * mm});
            skLineSegment(sketch, "E273.MirrorCS", {"start": v(188.5, -83.25) * mm, "end": v(201.5, -83.25) * mm});
            skLineSegment(sketch, "E274.MirrorCS", {"start": v(255.5, -101.25) * mm, "end": v(242.5, -101.25) * mm});
            skLineSegment(sketch, "E275.MirrorCS", {"start": v(255.5, -132.25) * mm, "end": v(242.5, -132.25) * mm});
            skLineSegment(sketch, "E276.MirrorCS", {"start": v(152.5, -132.25) * mm, "end": v(165.5, -132.25) * mm});
            skLineSegment(sketch, "E277.MirrorCS", {"start": v(152.5, -101.25) * mm, "end": v(165.5, -101.25) * mm});
            skLineSegment(sketch, "E278.MirrorCS", {"start": v(165.5, -101.25) * mm, "end": v(165.5, -114.25) * mm});
            skLineSegment(sketch, "E279.MirrorCS", {"start": v(170.5, -29.25) * mm, "end": v(170.5, -42.25) * mm});
            skLineSegment(sketch, "E280.MirrorCS", {"start": v(278.5, -47.25) * mm, "end": v(278.5, -60.25) * mm});
            skLineSegment(sketch, "E281.MirrorCS", {"start": v(278.5, -119.25) * mm, "end": v(278.5, -132.25) * mm});
            skLineSegment(sketch, "E282.MirrorCS", {"start": v(260.5, -65.25) * mm, "end": v(273.5, -65.25) * mm});
            skLineSegment(sketch, "E283.MirrorCS", {"start": v(237.5, -65.25) * mm, "end": v(237.5, -78.25) * mm});
            skLineSegment(sketch, "E284.MirrorCS", {"start": v(183.5, -42.25) * mm, "end": v(170.5, -42.25) * mm});
            skLineSegment(sketch, "E285.MirrorCS", {"start": v(165.5, -65.25) * mm, "end": v(165.5, -78.25) * mm});
            skLineSegment(sketch, "E286.MirrorCS", {"start": v(183.5, -65.25) * mm, "end": v(183.5, -78.25) * mm});
            skLineSegment(sketch, "E287.MirrorCS", {"start": v(188.5, -65.25) * mm, "end": v(201.5, -65.25) * mm});
            skLineSegment(sketch, "E288.MirrorCS", {"start": v(201.5, -119.25) * mm, "end": v(201.5, -132.25) * mm});
            skLineSegment(sketch, "E289.MirrorCS", {"start": v(152.5, -65.25) * mm, "end": v(165.5, -65.25) * mm});
            skLineSegment(sketch, "E290.MirrorCS", {"start": v(224.5, -132.25) * mm, "end": v(237.5, -132.25) * mm});
            skLineSegment(sketch, "E291.MirrorCS", {"start": v(224.5, -83.25) * mm, "end": v(237.5, -83.25) * mm});
            skLineSegment(sketch, "E292.MirrorCS", {"start": v(152.5, -47.25) * mm, "end": v(165.5, -47.25) * mm});
            skLineSegment(sketch, "E293.MirrorCS", {"start": v(219.5, -29.25) * mm, "end": v(206.5, -29.25) * mm});
            skLineSegment(sketch, "E294.MirrorCS", {"start": v(260.5, -65.25) * mm, "end": v(260.5, -78.25) * mm});
            skLineSegment(sketch, "E295.MirrorCS", {"start": v(224.5, -83.25) * mm, "end": v(224.5, -96.25) * mm});
            skLineSegment(sketch, "E296.MirrorCS", {"start": v(260.5, -29.25) * mm, "end": v(260.5, -42.25) * mm});
            skLineSegment(sketch, "E297.MirrorCS", {"start": v(188.5, -101.25) * mm, "end": v(188.5, -114.25) * mm});
            skLineSegment(sketch, "E298.MirrorCS", {"start": v(152.5, -119.25) * mm, "end": v(152.5, -132.25) * mm});
            skLineSegment(sketch, "E299.MirrorCS", {"start": v(219.5, -119.25) * mm, "end": v(206.5, -119.25) * mm});
            skLineSegment(sketch, "E300.MirrorCS", {"start": v(152.5, -83.25) * mm, "end": v(152.5, -96.25) * mm});
            skLineSegment(sketch, "E301.MirrorCS", {"start": v(255.5, -101.25) * mm, "end": v(255.5, -114.25) * mm});
            skLineSegment(sketch, "E302.MirrorCS", {"start": v(224.5, -60.25) * mm, "end": v(237.5, -60.25) * mm});
            skLineSegment(sketch, "E303.MirrorCS", {"start": v(188.5, -29.25) * mm, "end": v(201.5, -29.25) * mm});
            skLineSegment(sketch, "E304.MirrorCS", {"start": v(206.5, -119.25) * mm, "end": v(206.5, -132.25) * mm});
            skLineSegment(sketch, "E305.MirrorCS", {"start": v(188.5, -47.25) * mm, "end": v(188.5, -60.25) * mm});
            skLineSegment(sketch, "E306.MirrorCS", {"start": v(188.5, -78.25) * mm, "end": v(201.5, -78.25) * mm});
            skLineSegment(sketch, "E307.MirrorCS", {"start": v(255.5, -29.25) * mm, "end": v(242.5, -29.25) * mm});
            skLineSegment(sketch, "E308.MirrorCS", {"start": v(188.5, -42.25) * mm, "end": v(201.5, -42.25) * mm});
            skLineSegment(sketch, "E309.MirrorCS", {"start": v(206.5, -65.25) * mm, "end": v(206.5, -78.25) * mm});
            skLineSegment(sketch, "E310.MirrorCS", {"start": v(170.5, -119.25) * mm, "end": v(170.5, -132.25) * mm});
            skLineSegment(sketch, "E311.MirrorCS", {"start": v(255.5, -60.25) * mm, "end": v(242.5, -60.25) * mm});
            skLineSegment(sketch, "E312.MirrorCS", {"start": v(165.5, -47.25) * mm, "end": v(165.5, -60.25) * mm});
            skLineSegment(sketch, "E313.MirrorCS", {"start": v(183.5, -29.25) * mm, "end": v(170.5, -29.25) * mm});
            skLineSegment(sketch, "E314.MirrorCS", {"start": v(219.5, -47.25) * mm, "end": v(219.5, -60.25) * mm});
            skLineSegment(sketch, "E315.MirrorCS", {"start": v(183.5, -29.25) * mm, "end": v(183.5, -42.25) * mm});
            skLineSegment(sketch, "E316.MirrorCS", {"start": v(188.5, -60.25) * mm, "end": v(201.5, -60.25) * mm});
            skLineSegment(sketch, "E317.MirrorCS", {"start": v(152.5, -29.25) * mm, "end": v(152.5, -42.25) * mm});
            skLineSegment(sketch, "E318.MirrorCS", {"start": v(242.5, -65.25) * mm, "end": v(242.5, -78.25) * mm});
            skLineSegment(sketch, "E319.MirrorCS", {"start": v(255.5, -119.25) * mm, "end": v(242.5, -119.25) * mm});
            skLineSegment(sketch, "E320.MirrorCS", {"start": v(183.5, -83.25) * mm, "end": v(183.5, -96.25) * mm});
            skLineSegment(sketch, "E321.MirrorCS", {"start": v(291.5, -47.25) * mm, "end": v(278.5, -47.25) * mm});
            skLineSegment(sketch, "E322.MirrorCS", {"start": v(165.5, -83.25) * mm, "end": v(165.5, -96.25) * mm});
            skLineSegment(sketch, "E323.MirrorCS", {"start": v(291.5, -119.25) * mm, "end": v(278.5, -119.25) * mm});
            skLineSegment(sketch, "E324.MirrorCS", {"start": v(260.5, -83.25) * mm, "end": v(273.5, -83.25) * mm});
            skLineSegment(sketch, "E325.MirrorCS", {"start": v(255.5, -119.25) * mm, "end": v(255.5, -132.25) * mm});
            skLineSegment(sketch, "E326.MirrorCS", {"start": v(260.5, -47.25) * mm, "end": v(273.5, -47.25) * mm});
            skLineSegment(sketch, "E327.MirrorCS", {"start": v(224.5, -96.25) * mm, "end": v(237.5, -96.25) * mm});
            skLineSegment(sketch, "E328.MirrorCS", {"start": v(260.5, -29.25) * mm, "end": v(273.5, -29.25) * mm});
            skLineSegment(sketch, "E329.MirrorCS", {"start": v(224.5, -78.25) * mm, "end": v(237.5, -78.25) * mm});
            skLineSegment(sketch, "E330.MirrorCS", {"start": v(201.5, -83.25) * mm, "end": v(201.5, -96.25) * mm});
            skLineSegment(sketch, "E331.MirrorCS", {"start": v(183.5, -65.25) * mm, "end": v(170.5, -65.25) * mm});
            skLineSegment(sketch, "E332.MirrorCS", {"start": v(152.5, -47.25) * mm, "end": v(152.5, -60.25) * mm});
            skLineSegment(sketch, "E333.MirrorCS", {"start": v(219.5, -60.25) * mm, "end": v(206.5, -60.25) * mm});
            skLineSegment(sketch, "E334.MirrorCS", {"start": v(237.5, -83.25) * mm, "end": v(237.5, -96.25) * mm});
            skLineSegment(sketch, "E335.MirrorCS", {"start": v(188.5, -83.25) * mm, "end": v(188.5, -96.25) * mm});
            skLineSegment(sketch, "E336.MirrorCS", {"start": v(237.5, -101.25) * mm, "end": v(237.5, -114.25) * mm});
            skLineSegment(sketch, "E337.MirrorCS", {"start": v(278.5, -83.25) * mm, "end": v(278.5, -96.25) * mm});
            skLineSegment(sketch, "E338.MirrorCS", {"start": v(219.5, -78.25) * mm, "end": v(206.5, -78.25) * mm});
            skLineSegment(sketch, "E339.MirrorCS", {"start": v(152.5, -42.25) * mm, "end": v(165.5, -42.25) * mm});
            skLineSegment(sketch, "E340.MirrorCS", {"start": v(170.5, -65.25) * mm, "end": v(170.5, -78.25) * mm});
            skLineSegment(sketch, "E341.MirrorCS", {"start": v(255.5, -78.25) * mm, "end": v(242.5, -78.25) * mm});
            skLineSegment(sketch, "E342.MirrorCS", {"start": v(255.5, -114.25) * mm, "end": v(242.5, -114.25) * mm});
            skLineSegment(sketch, "E343.MirrorCS", {"start": v(273.5, -65.25) * mm, "end": v(273.5, -78.25) * mm});
            skLineSegment(sketch, "E344.MirrorCS", {"start": v(291.5, -132.25) * mm, "end": v(278.5, -132.25) * mm});
            skLineSegment(sketch, "E345.MirrorCS", {"start": v(291.5, -60.25) * mm, "end": v(278.5, -60.25) * mm});
            skLineSegment(sketch, "E346.MirrorCS", {"start": v(152.5, -119.25) * mm, "end": v(165.5, -119.25) * mm});
            skLineSegment(sketch, "E347.MirrorCS", {"start": v(188.5, -96.25) * mm, "end": v(201.5, -96.25) * mm});
            skLineSegment(sketch, "E348.MirrorCS", {"start": v(242.5, -47.25) * mm, "end": v(242.5, -60.25) * mm});
            skLineSegment(sketch, "E349.MirrorCS", {"start": v(165.5, -119.25) * mm, "end": v(165.5, -132.25) * mm});
            skLineSegment(sketch, "E350.MirrorCS", {"start": v(188.5, -47.25) * mm, "end": v(201.5, -47.25) * mm});
            skLineSegment(sketch, "E351.MirrorCS", {"start": v(260.5, -47.25) * mm, "end": v(260.5, -60.25) * mm});
            skLineSegment(sketch, "E352.MirrorCS", {"start": v(273.5, -101.25) * mm, "end": v(273.5, -114.25) * mm});
            skLineSegment(sketch, "E353.MirrorCS", {"start": v(183.5, -114.25) * mm, "end": v(170.5, -114.25) * mm});
            skLineSegment(sketch, "E354.MirrorCS", {"start": v(152.5, -29.25) * mm, "end": v(165.5, -29.25) * mm});
            skLineSegment(sketch, "E355.MirrorCS", {"start": v(224.5, -42.25) * mm, "end": v(237.5, -42.25) * mm});
            skLineSegment(sketch, "E356.MirrorCS", {"start": v(188.5, -114.25) * mm, "end": v(201.5, -114.25) * mm});
            skLineSegment(sketch, "E357.MirrorCS", {"start": v(291.5, -78.25) * mm, "end": v(278.5, -78.25) * mm});
            skLineSegment(sketch, "E358.MirrorCS", {"start": v(224.5, -114.25) * mm, "end": v(237.5, -114.25) * mm});
            skLineSegment(sketch, "E359.MirrorCS", {"start": v(183.5, -83.25) * mm, "end": v(170.5, -83.25) * mm});
            skLineSegment(sketch, "E360.MirrorCS", {"start": v(273.5, -47.25) * mm, "end": v(273.5, -60.25) * mm});
            skLineSegment(sketch, "E361.MirrorCS", {"start": v(152.5, -114.25) * mm, "end": v(165.5, -114.25) * mm});
            skLineSegment(sketch, "E362.MirrorCS", {"start": v(219.5, -65.25) * mm, "end": v(219.5, -78.25) * mm});
            skLineSegment(sketch, "E363.MirrorCS", {"start": v(255.5, -47.25) * mm, "end": v(255.5, -60.25) * mm});
            skLineSegment(sketch, "E364.MirrorCS", {"start": v(242.5, -83.25) * mm, "end": v(242.5, -96.25) * mm});
            skLineSegment(sketch, "E365.MirrorCS", {"start": v(260.5, -60.25) * mm, "end": v(273.5, -60.25) * mm});
            skLineSegment(sketch, "E366.MirrorCS", {"start": v(224.5, -65.25) * mm, "end": v(237.5, -65.25) * mm});
            skLineSegment(sketch, "E367.MirrorCS", {"start": v(183.5, -101.25) * mm, "end": v(183.5, -114.25) * mm});
            skLineSegment(sketch, "E368.MirrorCS", {"start": v(260.5, -78.25) * mm, "end": v(273.5, -78.25) * mm});
            skLineSegment(sketch, "E369.MirrorCS", {"start": v(219.5, -96.25) * mm, "end": v(206.5, -96.25) * mm});
            skLineSegment(sketch, "E370.MirrorCS", {"start": v(242.5, -101.25) * mm, "end": v(242.5, -114.25) * mm});
            skLineSegment(sketch, "E371", {"start": v(294, -21.56) * mm, "end": v(294, -144.75) * mm, "construction": true});
            skLineSegment(sketch, "E372.MirrorCS", {"start": v(309.5, -83.25) * mm, "end": v(309.5, -96.25) * mm});
            skLineSegment(sketch, "E373.MirrorCS", {"start": v(314.5, -29.25) * mm, "end": v(314.5, -42.25) * mm});
            skLineSegment(sketch, "E374.MirrorCS", {"start": v(327.5, -78.25) * mm, "end": v(314.5, -78.25) * mm});
            skLineSegment(sketch, "E375.MirrorCS", {"start": v(363.5, -47.25) * mm, "end": v(350.5, -47.25) * mm});
            skLineSegment(sketch, "E376.MirrorCS", {"start": v(368.5, -101.25) * mm, "end": v(381.5, -101.25) * mm});
            skLineSegment(sketch, "E377.MirrorCS", {"start": v(368.5, -65.25) * mm, "end": v(381.5, -65.25) * mm});
            skLineSegment(sketch, "E378.MirrorCS", {"start": v(332.5, -65.25) * mm, "end": v(345.5, -65.25) * mm});
            skLineSegment(sketch, "E379.MirrorCS", {"start": v(332.5, -101.25) * mm, "end": v(345.5, -101.25) * mm});
            skLineSegment(sketch, "E380.MirrorCS", {"start": v(363.5, -132.25) * mm, "end": v(350.5, -132.25) * mm});
            skLineSegment(sketch, "E381.MirrorCS", {"start": v(296.5, -119.25) * mm, "end": v(296.5, -132.25) * mm});
            skLineSegment(sketch, "E382.MirrorCS", {"start": v(332.5, -29.25) * mm, "end": v(332.5, -42.25) * mm});
            skLineSegment(sketch, "E383.MirrorCS", {"start": v(296.5, -83.25) * mm, "end": v(296.5, -96.25) * mm});
            skLineSegment(sketch, "E384.MirrorCS", {"start": v(332.5, -83.25) * mm, "end": v(345.5, -83.25) * mm});
            skLineSegment(sketch, "E385.MirrorCS", {"start": v(296.5, -119.25) * mm, "end": v(309.5, -119.25) * mm});
            skLineSegment(sketch, "E386.MirrorCS", {"start": v(332.5, -132.25) * mm, "end": v(345.5, -132.25) * mm});
            skLineSegment(sketch, "E387.MirrorCS", {"start": v(332.5, -29.25) * mm, "end": v(345.5, -29.25) * mm});
            skLineSegment(sketch, "E388.MirrorCS", {"start": v(327.5, -83.25) * mm, "end": v(327.5, -96.25) * mm});
            skLineSegment(sketch, "E389.MirrorCS", {"start": v(363.5, -101.25) * mm, "end": v(350.5, -101.25) * mm});
            skLineSegment(sketch, "E390.MirrorCS", {"start": v(350.5, -47.25) * mm, "end": v(350.5, -60.25) * mm});
            skLineSegment(sketch, "E391.MirrorCS", {"start": v(327.5, -47.25) * mm, "end": v(327.5, -60.25) * mm});
            skLineSegment(sketch, "E392.MirrorCS", {"start": v(332.5, -119.25) * mm, "end": v(345.5, -119.25) * mm});
            skLineSegment(sketch, "E393.MirrorCS", {"start": v(363.5, -29.25) * mm, "end": v(350.5, -29.25) * mm});
            skLineSegment(sketch, "E394.MirrorCS", {"start": v(296.5, -101.25) * mm, "end": v(309.5, -101.25) * mm});
            skLineSegment(sketch, "E395.MirrorCS", {"start": v(368.5, -83.25) * mm, "end": v(381.5, -83.25) * mm});
            skLineSegment(sketch, "E396.MirrorCS", {"start": v(327.5, -96.25) * mm, "end": v(314.5, -96.25) * mm});
            skLineSegment(sketch, "E397.MirrorCS", {"start": v(314.5, -83.25) * mm, "end": v(314.5, -96.25) * mm});
            skLineSegment(sketch, "E398.MirrorCS", {"start": v(327.5, -83.25) * mm, "end": v(314.5, -83.25) * mm});
            skLineSegment(sketch, "E399.MirrorCS", {"start": v(296.5, -114.25) * mm, "end": v(309.5, -114.25) * mm});
            skLineSegment(sketch, "E400.MirrorCS", {"start": v(350.5, -29.25) * mm, "end": v(350.5, -42.25) * mm});
            skLineSegment(sketch, "E401.MirrorCS", {"start": v(381.5, -29.25) * mm, "end": v(381.5, -42.25) * mm});
            skLineSegment(sketch, "E402.MirrorCS", {"start": v(309.5, -119.25) * mm, "end": v(309.5, -132.25) * mm});
            skLineSegment(sketch, "E403.MirrorCS", {"start": v(368.5, -42.25) * mm, "end": v(381.5, -42.25) * mm});
            skLineSegment(sketch, "E404.MirrorCS", {"start": v(363.5, -29.25) * mm, "end": v(363.5, -42.25) * mm});
            skLineSegment(sketch, "E405.MirrorCS", {"start": v(314.5, -119.25) * mm, "end": v(314.5, -132.25) * mm});
            skLineSegment(sketch, "E406.MirrorCS", {"start": v(296.5, -60.25) * mm, "end": v(309.5, -60.25) * mm});
            skLineSegment(sketch, "E407.MirrorCS", {"start": v(314.5, -101.25) * mm, "end": v(314.5, -114.25) * mm});
            skLineSegment(sketch, "E408.MirrorCS", {"start": v(363.5, -78.25) * mm, "end": v(350.5, -78.25) * mm});
            skLineSegment(sketch, "E409.MirrorCS", {"start": v(350.5, -101.25) * mm, "end": v(350.5, -114.25) * mm});
            skLineSegment(sketch, "E410.MirrorCS", {"start": v(296.5, -65.25) * mm, "end": v(309.5, -65.25) * mm});
            skLineSegment(sketch, "E411.MirrorCS", {"start": v(327.5, -65.25) * mm, "end": v(314.5, -65.25) * mm});
            skLineSegment(sketch, "E412.MirrorCS", {"start": v(327.5, -101.25) * mm, "end": v(327.5, -114.25) * mm});
            skLineSegment(sketch, "E413.MirrorCS", {"start": v(327.5, -132.25) * mm, "end": v(314.5, -132.25) * mm});
            skLineSegment(sketch, "E414.MirrorCS", {"start": v(368.5, -47.25) * mm, "end": v(368.5, -60.25) * mm});
            skLineSegment(sketch, "E415.MirrorCS", {"start": v(368.5, -65.25) * mm, "end": v(368.5, -78.25) * mm});
            skLineSegment(sketch, "E416.MirrorCS", {"start": v(296.5, -65.25) * mm, "end": v(296.5, -78.25) * mm});
            skLineSegment(sketch, "E417.MirrorCS", {"start": v(327.5, -42.25) * mm, "end": v(314.5, -42.25) * mm});
            skLineSegment(sketch, "E418.MirrorCS", {"start": v(327.5, -119.25) * mm, "end": v(327.5, -132.25) * mm});
            skLineSegment(sketch, "E419.MirrorCS", {"start": v(327.5, -101.25) * mm, "end": v(314.5, -101.25) * mm});
            skLineSegment(sketch, "E420.MirrorCS", {"start": v(296.5, -101.25) * mm, "end": v(296.5, -114.25) * mm});
            skLineSegment(sketch, "E421.MirrorCS", {"start": v(350.5, -65.25) * mm, "end": v(350.5, -78.25) * mm});
            skLineSegment(sketch, "E422.MirrorCS", {"start": v(381.5, -83.25) * mm, "end": v(381.5, -96.25) * mm});
            skLineSegment(sketch, "E423.MirrorCS", {"start": v(327.5, -119.25) * mm, "end": v(314.5, -119.25) * mm});
            skLineSegment(sketch, "E424.MirrorCS", {"start": v(368.5, -119.25) * mm, "end": v(381.5, -119.25) * mm});
            skLineSegment(sketch, "E425.MirrorCS", {"start": v(332.5, -47.25) * mm, "end": v(332.5, -60.25) * mm});
            skLineSegment(sketch, "E426.MirrorCS", {"start": v(332.5, -83.25) * mm, "end": v(332.5, -96.25) * mm});
            skLineSegment(sketch, "E427.MirrorCS", {"start": v(350.5, -119.25) * mm, "end": v(350.5, -132.25) * mm});
            skLineSegment(sketch, "E428.MirrorCS", {"start": v(363.5, -47.25) * mm, "end": v(363.5, -60.25) * mm});
            skLineSegment(sketch, "E429.MirrorCS", {"start": v(368.5, -29.25) * mm, "end": v(368.5, -42.25) * mm});
            skLineSegment(sketch, "E430.MirrorCS", {"start": v(345.5, -47.25) * mm, "end": v(345.5, -60.25) * mm});
            skLineSegment(sketch, "E431.MirrorCS", {"start": v(314.5, -65.25) * mm, "end": v(314.5, -78.25) * mm});
            skLineSegment(sketch, "E432.MirrorCS", {"start": v(332.5, -60.25) * mm, "end": v(345.5, -60.25) * mm});
            skLineSegment(sketch, "E433.MirrorCS", {"start": v(363.5, -83.25) * mm, "end": v(363.5, -96.25) * mm});
            skLineSegment(sketch, "E434.MirrorCS", {"start": v(381.5, -101.25) * mm, "end": v(381.5, -114.25) * mm});
            skLineSegment(sketch, "E435.MirrorCS", {"start": v(332.5, -47.25) * mm, "end": v(345.5, -47.25) * mm});
            skLineSegment(sketch, "E436.MirrorCS", {"start": v(363.5, -96.25) * mm, "end": v(350.5, -96.25) * mm});
            skLineSegment(sketch, "E437.MirrorCS", {"start": v(332.5, -65.25) * mm, "end": v(332.5, -78.25) * mm});
            skLineSegment(sketch, "E438.MirrorCS", {"start": v(309.5, -101.25) * mm, "end": v(309.5, -114.25) * mm});
            skLineSegment(sketch, "E439.MirrorCS", {"start": v(345.5, -83.25) * mm, "end": v(345.5, -96.25) * mm});
            skLineSegment(sketch, "E440.MirrorCS", {"start": v(296.5, -47.25) * mm, "end": v(296.5, -60.25) * mm});
            skLineSegment(sketch, "E441.MirrorCS", {"start": v(368.5, -119.25) * mm, "end": v(368.5, -132.25) * mm});
            skLineSegment(sketch, "E442.MirrorCS", {"start": v(368.5, -47.25) * mm, "end": v(381.5, -47.25) * mm});
            skLineSegment(sketch, "E443.MirrorCS", {"start": v(381.5, -47.25) * mm, "end": v(381.5, -60.25) * mm});
            skLineSegment(sketch, "E444.MirrorCS", {"start": v(368.5, -60.25) * mm, "end": v(381.5, -60.25) * mm});
            skLineSegment(sketch, "E445.MirrorCS", {"start": v(332.5, -101.25) * mm, "end": v(332.5, -114.25) * mm});
            skLineSegment(sketch, "E446.MirrorCS", {"start": v(327.5, -60.25) * mm, "end": v(314.5, -60.25) * mm});
            skLineSegment(sketch, "E447.MirrorCS", {"start": v(309.5, -47.25) * mm, "end": v(309.5, -60.25) * mm});
            skLineSegment(sketch, "E448.MirrorCS", {"start": v(296.5, -96.25) * mm, "end": v(309.5, -96.25) * mm});
            skLineSegment(sketch, "E449.MirrorCS", {"start": v(363.5, -114.25) * mm, "end": v(350.5, -114.25) * mm});
            skLineSegment(sketch, "E450.MirrorCS", {"start": v(332.5, -114.25) * mm, "end": v(345.5, -114.25) * mm});
            skLineSegment(sketch, "E451.MirrorCS", {"start": v(327.5, -65.25) * mm, "end": v(327.5, -78.25) * mm});
            skLineSegment(sketch, "E452.MirrorCS", {"start": v(309.5, -29.25) * mm, "end": v(309.5, -42.25) * mm});
            skLineSegment(sketch, "E453.MirrorCS", {"start": v(345.5, -29.25) * mm, "end": v(345.5, -42.25) * mm});
            skLineSegment(sketch, "E454.MirrorCS", {"start": v(327.5, -47.25) * mm, "end": v(314.5, -47.25) * mm});
            skLineSegment(sketch, "E455.MirrorCS", {"start": v(309.5, -65.25) * mm, "end": v(309.5, -78.25) * mm});
            skLineSegment(sketch, "E456.MirrorCS", {"start": v(368.5, -114.25) * mm, "end": v(381.5, -114.25) * mm});
            skLineSegment(sketch, "E457.MirrorCS", {"start": v(296.5, -29.25) * mm, "end": v(296.5, -42.25) * mm});
            skLineSegment(sketch, "E458.MirrorCS", {"start": v(368.5, -101.25) * mm, "end": v(368.5, -114.25) * mm});
            skLineSegment(sketch, "E459.MirrorCS", {"start": v(332.5, -42.25) * mm, "end": v(345.5, -42.25) * mm});
            skLineSegment(sketch, "E460.MirrorCS", {"start": v(381.5, -119.25) * mm, "end": v(381.5, -132.25) * mm});
            skLineSegment(sketch, "E461.MirrorCS", {"start": v(363.5, -119.25) * mm, "end": v(350.5, -119.25) * mm});
            skLineSegment(sketch, "E462.MirrorCS", {"start": v(332.5, -96.25) * mm, "end": v(345.5, -96.25) * mm});
            skLineSegment(sketch, "E463.MirrorCS", {"start": v(363.5, -83.25) * mm, "end": v(350.5, -83.25) * mm});
            skLineSegment(sketch, "E464.MirrorCS", {"start": v(363.5, -42.25) * mm, "end": v(350.5, -42.25) * mm});
            skLineSegment(sketch, "E465.MirrorCS", {"start": v(314.5, -47.25) * mm, "end": v(314.5, -60.25) * mm});
            skLineSegment(sketch, "E466.MirrorCS", {"start": v(332.5, -78.25) * mm, "end": v(345.5, -78.25) * mm});
            skLineSegment(sketch, "E467.MirrorCS", {"start": v(296.5, -78.25) * mm, "end": v(309.5, -78.25) * mm});
            skLineSegment(sketch, "E468.MirrorCS", {"start": v(368.5, -29.25) * mm, "end": v(381.5, -29.25) * mm});
            skLineSegment(sketch, "E469.MirrorCS", {"start": v(332.5, -119.25) * mm, "end": v(332.5, -132.25) * mm});
            skLineSegment(sketch, "E470.MirrorCS", {"start": v(381.5, -65.25) * mm, "end": v(381.5, -78.25) * mm});
            skLineSegment(sketch, "E471.MirrorCS", {"start": v(296.5, -83.25) * mm, "end": v(309.5, -83.25) * mm});
            skLineSegment(sketch, "E472.MirrorCS", {"start": v(296.5, -29.25) * mm, "end": v(309.5, -29.25) * mm});
            skLineSegment(sketch, "E473.MirrorCS", {"start": v(327.5, -29.25) * mm, "end": v(327.5, -42.25) * mm});
            skLineSegment(sketch, "E474.MirrorCS", {"start": v(296.5, -47.25) * mm, "end": v(309.5, -47.25) * mm});
            skLineSegment(sketch, "E475.MirrorCS", {"start": v(368.5, -96.25) * mm, "end": v(381.5, -96.25) * mm});
            skLineSegment(sketch, "E476.MirrorCS", {"start": v(296.5, -42.25) * mm, "end": v(309.5, -42.25) * mm});
            skLineSegment(sketch, "E477.MirrorCS", {"start": v(368.5, -132.25) * mm, "end": v(381.5, -132.25) * mm});
            skLineSegment(sketch, "E478.MirrorCS", {"start": v(363.5, -119.25) * mm, "end": v(363.5, -132.25) * mm});
            skLineSegment(sketch, "E479.MirrorCS", {"start": v(363.5, -65.25) * mm, "end": v(350.5, -65.25) * mm});
            skLineSegment(sketch, "E480.MirrorCS", {"start": v(345.5, -65.25) * mm, "end": v(345.5, -78.25) * mm});
            skLineSegment(sketch, "E481.MirrorCS", {"start": v(363.5, -60.25) * mm, "end": v(350.5, -60.25) * mm});
            skLineSegment(sketch, "E482.MirrorCS", {"start": v(368.5, -83.25) * mm, "end": v(368.5, -96.25) * mm});
            skLineSegment(sketch, "E483.MirrorCS", {"start": v(350.5, -83.25) * mm, "end": v(350.5, -96.25) * mm});
            skLineSegment(sketch, "E484.MirrorCS", {"start": v(345.5, -119.25) * mm, "end": v(345.5, -132.25) * mm});
            skLineSegment(sketch, "E485.MirrorCS", {"start": v(296.5, -132.25) * mm, "end": v(309.5, -132.25) * mm});
            skLineSegment(sketch, "E486.MirrorCS", {"start": v(368.5, -78.25) * mm, "end": v(381.5, -78.25) * mm});
            skLineSegment(sketch, "E487.MirrorCS", {"start": v(363.5, -101.25) * mm, "end": v(363.5, -114.25) * mm});
            skLineSegment(sketch, "E488.MirrorCS", {"start": v(345.5, -101.25) * mm, "end": v(345.5, -114.25) * mm});
            skLineSegment(sketch, "E489.MirrorCS", {"start": v(363.5, -65.25) * mm, "end": v(363.5, -78.25) * mm});
            skLineSegment(sketch, "E490.MirrorCS", {"start": v(327.5, -29.25) * mm, "end": v(314.5, -29.25) * mm});
            skLineSegment(sketch, "E491.MirrorCS", {"start": v(327.5, -114.25) * mm, "end": v(314.5, -114.25) * mm});
            skCircle(sketch, "E492", {"center": v(32.44, -141.9) * mm, "radius": 1.5 * mm});
            skCircle(sketch, "E493", {"center": v(141.27, -141.9) * mm, "radius": 1.5 * mm});
            skCircle(sketch, "E494", {"center": v(248.81, -141.9) * mm, "radius": 1.5 * mm});
            skCircle(sketch, "E495", {"center": v(357.84, -141.9) * mm, "radius": 1.5 * mm});
            skCircle(sketch, "E496", {"center": v(32.44, -20) * mm, "radius": 1.5 * mm});
            skCircle(sketch, "E497", {"center": v(115, -20) * mm, "radius": 1.5 * mm});
            skCircle(sketch, "E498", {"center": v(248.81, -20) * mm, "radius": 1.5 * mm});
            skCircle(sketch, "E499", {"center": v(350.5, -20) * mm, "radius": 1.5 * mm});
            skSolve(sketch);
        }
        {
            var Q0;
            Q0=qSketchRegion(id+"F0",true);
            extrude(context, id + "F1", {"entities" : qUnion([Q0]), "depth" : 3 * mm});
        }
        {
            var Q0;
            Q0=qCreatedBy(makeId("Top.planeOp"),FACE);
            var sketch = newSketch(context, id + "F2", { "sketchPlane" : qUnion([Q0])});
            skLineSegment(sketch, "E500.bottom", {"start": v(0, 0) * mm, "end": v(390, 0) * mm});
            skLineSegment(sketch, "E500.top", {"start": v(0, -150) * mm, "end": v(390, -150) * mm});
            skLineSegment(sketch, "E500.left", {"start": v(0, 0) * mm, "end": v(0, -150) * mm});
            skLineSegment(sketch, "E500.right", {"start": v(390, 0) * mm, "end": v(390, -150) * mm});
            skCircle(sketch, "E501", {"center": v(32.44, -20) * mm, "radius": 1.5 * mm});
            skCircle(sketch, "E502", {"center": v(115, -20) * mm, "radius": 1.5 * mm});
            skCircle(sketch, "E503", {"center": v(248.81, -20) * mm, "radius": 1.5 * mm});
            skCircle(sketch, "E504", {"center": v(350.5, -20) * mm, "radius": 1.5 * mm});
            skCircle(sketch, "E505", {"center": v(32.44, -141.9) * mm, "radius": 1.5 * mm});
            skCircle(sketch, "E506", {"center": v(141.27, -141.9) * mm, "radius": 1.5 * mm});
            skCircle(sketch, "E507", {"center": v(248.81, -141.9) * mm, "radius": 1.5 * mm});
            skCircle(sketch, "E508", {"center": v(357.84, -141.9) * mm, "radius": 1.5 * mm});
            skSolve(sketch);
        }
        {
            var Q0;
            Q0=qSketchRegion(id+"F2",true);
            extrude(context, id + "F3", {"entities" : qUnion([Q0]), "oppositeDirection" : true, "depth" : 2 * mm});
        }
        {
            var Q0;
            Q0=qCreatedBy(makeId("Top.planeOp"),FACE);
            var sketch = newSketch(context, id + "F4", { "sketchPlane" : qUnion([Q0])});
            skLineSegment(sketch, "E509.bottom", {"start": v(0, 0) * mm, "end": v(390, 0) * mm});
            skLineSegment(sketch, "E509.top", {"start": v(0, -150) * mm, "end": v(390, -150) * mm});
            skLineSegment(sketch, "E509.left", {"start": v(0, 0) * mm, "end": v(0, -150) * mm});
            skLineSegment(sketch, "E509.right", {"start": v(390, 0) * mm, "end": v(390, -150) * mm});
            skLineSegment(sketch, "E510.bottom", {"start": v(2, -2) * mm, "end": v(388, -2) * mm});
            skLineSegment(sketch, "E510.top", {"start": v(2, -148) * mm, "end": v(388, -148) * mm});
            skLineSegment(sketch, "E510.left", {"start": v(2, -2) * mm, "end": v(2, -148) * mm});
            skLineSegment(sketch, "E510.right", {"start": v(388, -2) * mm, "end": v(388, -148) * mm});
            skSolve(sketch);
        }
        {
            var Q0;
            Q0 = qSketchRegion(id + "F4", true);
            extrude(context, id + "F5", {"entities" : qUnion([Q0]), "oppositeDirection" : true, "depth" : 250 * mm});
        }
    });
